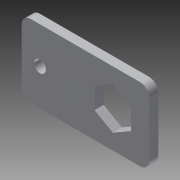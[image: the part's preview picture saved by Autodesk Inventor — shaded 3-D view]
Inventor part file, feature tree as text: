
AUTODESK INVENTOR PART (.ipt)
format: ipt  version: 2014 (Build 180170000, 170)  size: 95,744 bytes
history: native  units: in
note: dims shown in document units (in); Inventor stores cm internally (conversion verified against a paired STEP export)
features: extrude x1, fillet x1, sketch x1
ambient origin geometry x8: Origin, YZ Plane, XZ Plane, XY Plane, X Axis, Y Axis, Z Axis, Center Point
bodies: Solid1 (feature_tree)
feature tree (3):
  extrude  "Extrusion1"  Depth=1.0in
  fillet  "Fillet1"  Radius=0.163in
  sketch  "Sketch1"  dims[d0=1.75in d1=1.0in d2=0.163in d3=0.5in d4=0.25in d5=1.0in d6=0.5in d7=0.5in d8=0.125in d9=0.0in d10=0.125in]
